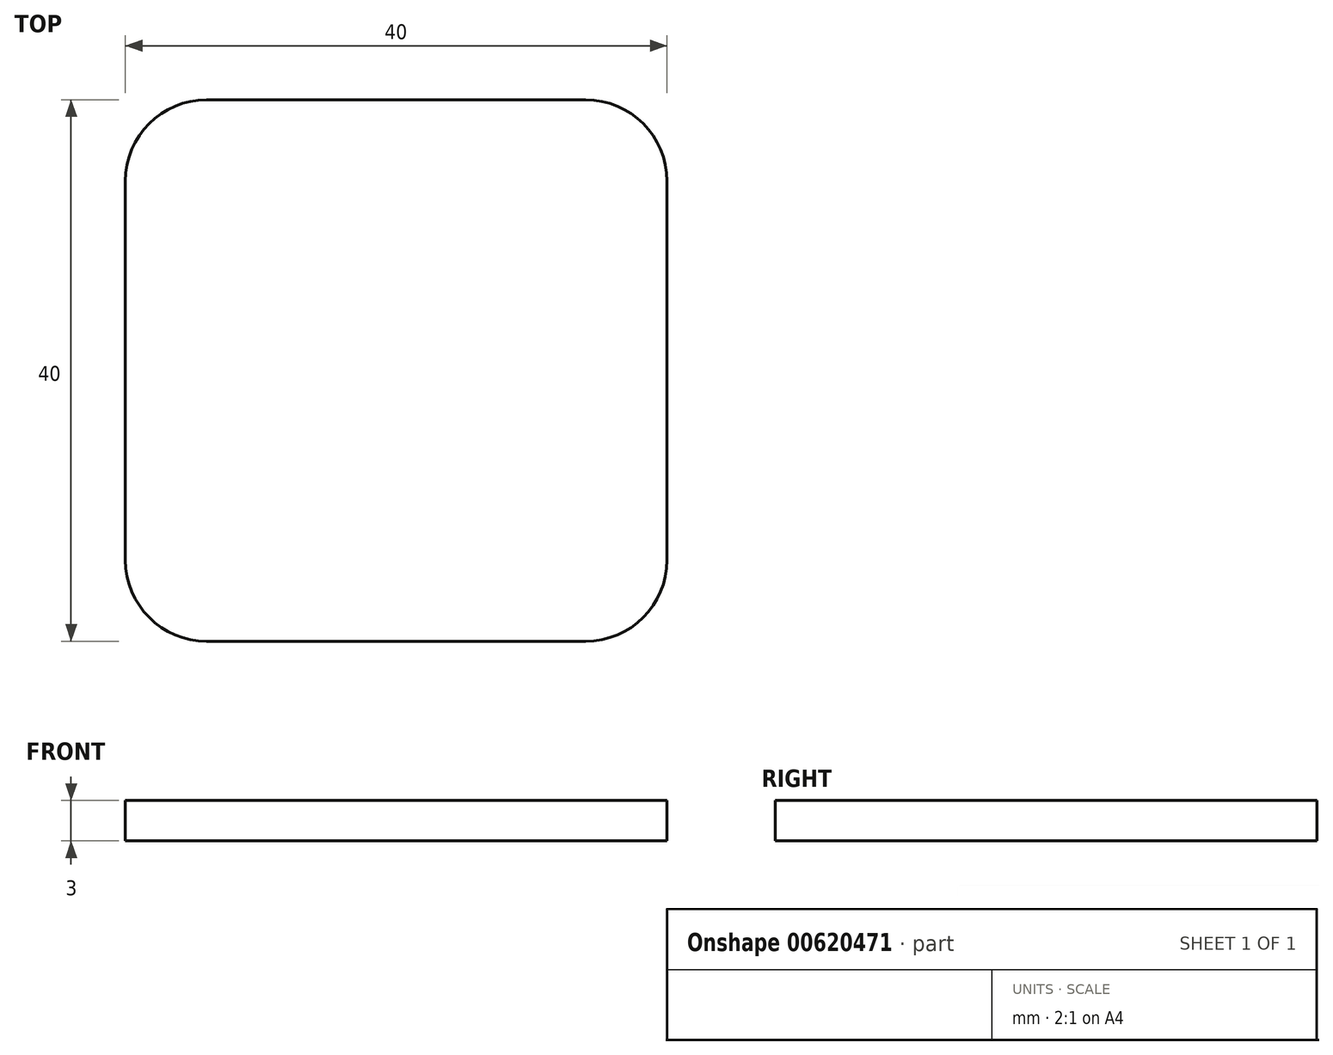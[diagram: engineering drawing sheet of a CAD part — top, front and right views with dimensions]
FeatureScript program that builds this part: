
annotation { "Feature Type Name" : "Feature", "Feature Type Description" : "" }
export const myFeature = defineFeature(function(context is Context, id is Id, definition is map)
    precondition{}
    {
        {
            var Q0;
            Q0=qCreatedBy(makeId("Top.planeOp"),FACE);
            var sketch = newSketch(context, id + "F0", { "sketchPlane" : qUnion([Q0])});
            skLineSegment(sketch, "E0.bottom", {"start": v(20, 20) * mm, "end": v(-20, 20) * mm});
            skLineSegment(sketch, "E0.top", {"start": v(20, -20) * mm, "end": v(-20, -20) * mm});
            skLineSegment(sketch, "E0.left", {"start": v(20, 20) * mm, "end": v(20, -20) * mm});
            skLineSegment(sketch, "E0.right", {"start": v(-20, 20) * mm, "end": v(-20, -20) * mm});
            skPoint(sketch, "E0.middle", {"position": v(0, 0) * mm});
            skSolve(sketch);
        }
        {
            var Q0;
            Q0=makeQuery(id+"F0.imprint","IMPRINT",FACE,{"disambiguationData":[TD([[makeQuery(id+"F0.imprint","IMPRINT",EDGE,{"derivedFrom":sQuery(id+"F0.wireOp",EDGE,"E0.bottom")}),1.0]])]});
            extrude(context, id + "F1", {"entities" : qUnion([Q0]), "depth" : 3 * mm, "offsetDistance" : 25 * mm});
        }
        {
            var Q0;
            Q0=makeQuery(id+"F1.opExtrude","SWEPT_EDGE",EDGE,{"disambiguationData":[OSD([sQuery(id+"F0.wireOp",EDGE,"E0.top"),sQuery(id+"F0.wireOp",EDGE,"E0.left")])]});
            var Q1;
            Q1=makeQuery(id+"F1.opExtrude","SWEPT_EDGE",EDGE,{"disambiguationData":[OSD([sQuery(id+"F0.wireOp",EDGE,"E0.bottom"),sQuery(id+"F0.wireOp",EDGE,"E0.left")])]});
            var Q2;
            Q2=makeQuery(id+"F1.opExtrude","SWEPT_EDGE",EDGE,{"disambiguationData":[OSD([sQuery(id+"F0.wireOp",EDGE,"E0.bottom"),sQuery(id+"F0.wireOp",EDGE,"E0.right")])]});
            var Q3;
            Q3=makeQuery(id+"F1.opExtrude","SWEPT_EDGE",EDGE,{"disambiguationData":[OSD([sQuery(id+"F0.wireOp",EDGE,"E0.top"),sQuery(id+"F0.wireOp",EDGE,"E0.right")])]});
            fillet(context, id + "F2", {"entities" : qUnion([Q0, Q1, Q2, Q3]), "radius" : 6 * mm, "tangentPropagation" : true, "allowEdgeOverflow" : false});
        }
    });
